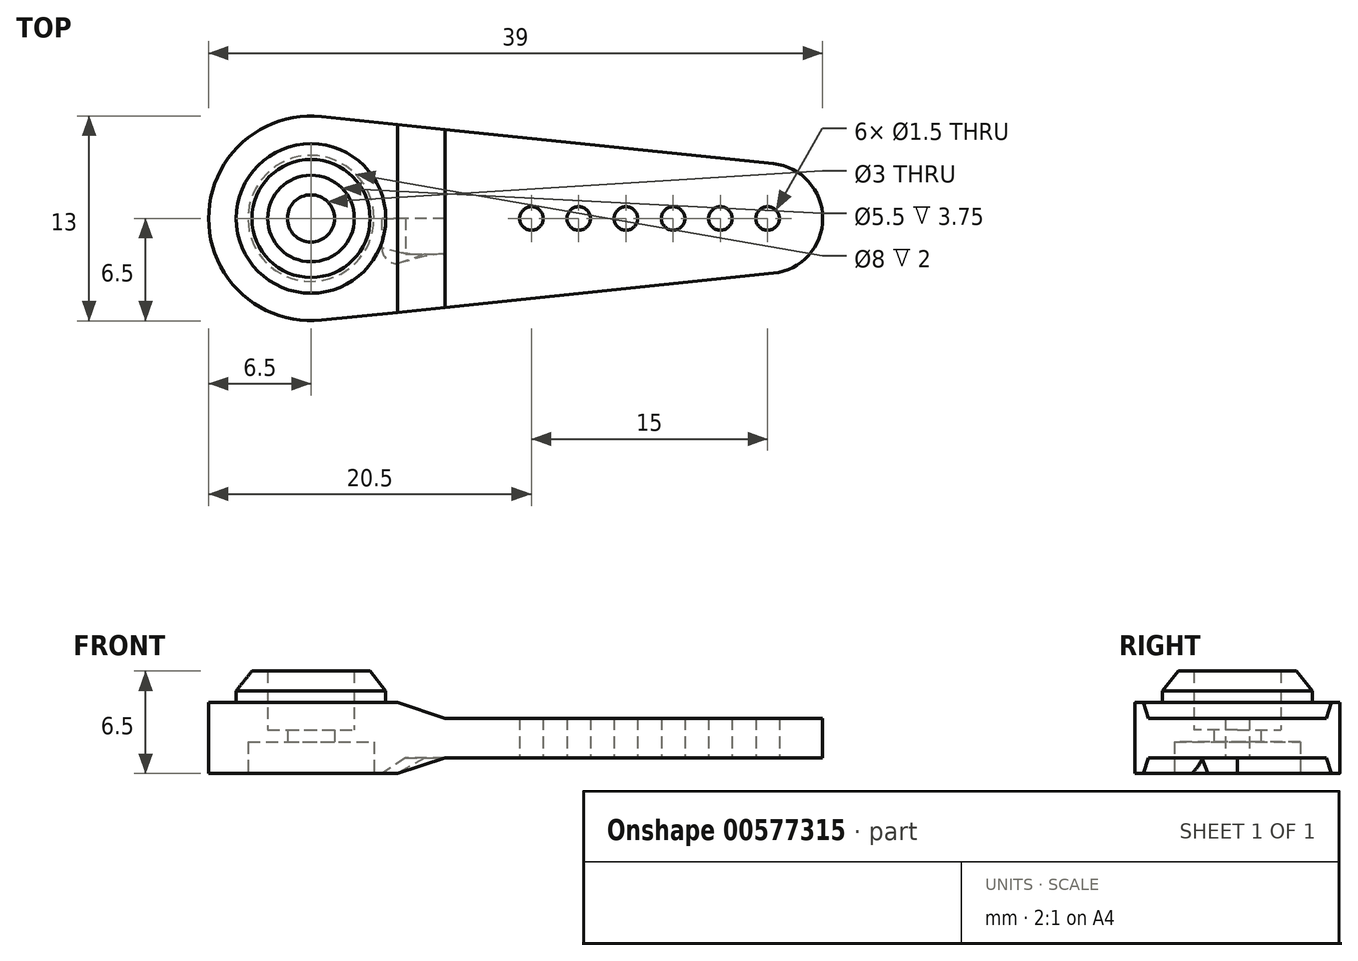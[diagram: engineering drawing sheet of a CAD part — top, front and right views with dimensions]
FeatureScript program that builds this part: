
annotation { "Feature Type Name" : "Feature", "Feature Type Description" : "" }
export const myFeature = defineFeature(function(context is Context, id is Id, definition is map)
    precondition{}
    {
        {
            var Q0;
            Q0=qCreatedBy(makeId("Top.planeOp"),FACE);
            var sketch = newSketch(context, id + "F0", { "sketchPlane" : qUnion([Q0])});
            skLineSegment(sketch, "E0.bottom", {"start": v(0, 0) * mm, "end": v(39, 0) * mm, "construction": true});
            skLineSegment(sketch, "E0.top", {"start": v(0, 13) * mm, "end": v(39, 13) * mm, "construction": true});
            skLineSegment(sketch, "E0.left", {"start": v(0, 0) * mm, "end": v(0, 13) * mm, "construction": true});
            skLineSegment(sketch, "E0.right", {"start": v(39, 0) * mm, "end": v(39, 13) * mm, "construction": true});
            skCircle(sketch, "E1", {"center": v(6.5, 6.5) * mm, "radius": 6.5 * mm});
            skPoint(sketch, "E1.first.point", {"position": v(0, 6.5) * mm});
            skPoint(sketch, "E1.second.point", {"position": v(6.5, 13) * mm});
            skPoint(sketch, "E1.third.point", {"position": v(6.5, 0) * mm});
            skCircle(sketch, "E2", {"center": v(35.5, 6.5) * mm, "radius": 3.5 * mm});
            skLineSegment(sketch, "E3", {"start": v(35.86, 9.98) * mm, "end": v(7.17, 12.97) * mm});
            skLineSegment(sketch, "E4", {"start": v(35.86, 3.02) * mm, "end": v(7.17, 0.03) * mm});
            skCircle(sketch, "E5", {"center": v(35.5, 6.5) * mm, "radius": 0.75 * mm});
            skCircle(sketch, "E6.1.0.0", {"center": v(32.5, 6.5) * mm, "radius": 0.75 * mm});
            skCircle(sketch, "E6.2.0.0", {"center": v(29.5, 6.5) * mm, "radius": 0.75 * mm});
            skCircle(sketch, "E6.3.0.0", {"center": v(26.5, 6.5) * mm, "radius": 0.75 * mm});
            skCircle(sketch, "E6.4.0.0", {"center": v(23.5, 6.5) * mm, "radius": 0.75 * mm});
            skCircle(sketch, "E6.5.0.0", {"center": v(20.5, 6.5) * mm, "radius": 0.75 * mm});
            skLineSegment(sketch, "E6.direction1", {"start": v(35.5, 6.5) * mm, "end": v(32.5, 6.5) * mm, "construction": true});
            skCircle(sketch, "E7", {"center": v(6.5, 6.5) * mm, "radius": 1.5 * mm});
            skSolve(sketch);
        }
        {
            var Q0;
            Q0 = qSketchRegion(id + "F0", true);
            extrude(context, id + "F1", {"entities" : qUnion([Q0]), "depth" : 4.5 * mm, "offsetDistance" : 25 * mm});
        }
        {
            var Q0;
            Q0=qCreatedBy(makeId("Front.planeOp"),FACE);
            var sketch = newSketch(context, id + "F2", { "sketchPlane" : qUnion([Q0])});
            skLineSegment(sketch, "E8", {"start": v(0, 0) * mm, "end": v(0, 2.25) * mm, "construction": true});
            skLineSegment(sketch, "E9", {"start": v(0, 2.25) * mm, "end": v(39, 2.25) * mm, "construction": true});
            skLineSegment(sketch, "E10", {"start": v(39, 2.25) * mm, "end": v(39, 1) * mm, "construction": true});
            skLineSegment(sketch, "E11", {"start": v(0, 0) * mm, "end": v(12, 0) * mm, "construction": true});
            skLineSegment(sketch, "E12", {"start": v(12, 0) * mm, "end": v(15, 1) * mm});
            skLineSegment(sketch, "E13", {"start": v(15, 1) * mm, "end": v(39, 1) * mm});
            skLineSegment(sketch, "E14.MirrorCS", {"start": v(12, 4.5) * mm, "end": v(15, 3.5) * mm});
            skLineSegment(sketch, "E15.MirrorCS", {"start": v(15, 3.5) * mm, "end": v(39, 3.5) * mm});
            skLineSegment(sketch, "E16.MirrorCS", {"start": v(39, 2.25) * mm, "end": v(39, 3.5) * mm, "construction": true});
            skLineSegment(sketch, "E17.MirrorCS", {"start": v(0, 4.5) * mm, "end": v(12, 4.5) * mm, "construction": true});
            skLineSegment(sketch, "E18.MirrorCS", {"start": v(0, 4.5) * mm, "end": v(0, 2.25) * mm, "construction": true});
            skLineSegment(sketch, "E19", {"start": v(12, 4.5) * mm, "end": v(39, 4.5) * mm});
            skLineSegment(sketch, "E20", {"start": v(39, 4.5) * mm, "end": v(39, 3.5) * mm});
            skLineSegment(sketch, "E21", {"start": v(12, 0) * mm, "end": v(39, 0) * mm});
            skLineSegment(sketch, "E22", {"start": v(39, 0) * mm, "end": v(39, 1) * mm});
            skSolve(sketch);
        }
        {
            var Q0;
            Q0 = qSketchRegion(id + "F2", true);
            extrude(context, id + "F3", {"entities" : qUnion([Q0]), "operationType" : NewBodyOperationType.REMOVE, "endBound" : BoundingType.THROUGH_ALL, "oppositeDirection" : true, "depth" : 25 * mm, "offsetDistance" : 25 * mm});
        }
        {
            var Q0;
            Q0=makeQuery(id+"F1.opExtrude","CAP_FACE",FACE,{"disambiguationData":[OSD([sQuery(id+"F0.wireOp",EDGE,"E1"),sQuery(id+"F0.wireOp",EDGE,"E2"),sQuery(id+"F0.wireOp",EDGE,"E3"),sQuery(id+"F0.wireOp",EDGE,"E4"),sQuery(id+"F0.wireOp",EDGE,"E5"),sQuery(id+"F0.wireOp",EDGE,"E6.1.0.0"),sQuery(id+"F0.wireOp",EDGE,"E6.2.0.0"),sQuery(id+"F0.wireOp",EDGE,"E6.3.0.0"),sQuery(id+"F0.wireOp",EDGE,"E6.4.0.0"),sQuery(id+"F0.wireOp",EDGE,"E6.5.0.0"),sQuery(id+"F0.wireOp",EDGE,"E7")])],"isStart":false});
            var sketch = newSketch(context, id + "F4", { "sketchPlane" : qUnion([Q0])});
            skCircle(sketch, "E23", {"center": v(6.5, 6.5) * mm, "radius": 4.75 * mm});
            skCircle(sketch, "E24", {"center": v(6.5, 6.5) * mm, "radius": 2.75 * mm});
            skSolve(sketch);
        }
        {
            var Q0;
            Q0 = qSketchRegion(id + "F4", true);
            extrude(context, id + "F5", {"entities" : qUnion([Q0]), "operationType" : NewBodyOperationType.ADD, "depth" : .75 * mm, "offsetDistance" : 25 * mm});
        }
        {
            var Q0;
            Q0=qCreatedBy(makeId("Front.planeOp"),FACE);
            cPlane(context, id + "F6", {"entities" : qUnion([Q0]), "cplaneType" : CPlaneType.OFFSET, "offset" : 6.5 * mm, "oppositeDirection" : true, "width" : 150 * mm, "height" : 150 * mm});
        }
        {
            var Q0;
            Q0=qCreatedBy(id+"F6.planeOp",FACE);
            var sketch = newSketch(context, id + "F7", { "sketchPlane" : qUnion([Q0])});
            skLineSegment(sketch, "E25.0", {"start": v(1.75, 5.25) * mm, "end": v(11.25, 5.25) * mm, "construction": true});
            skLineSegment(sketch, "E26", {"start": v(11.25, 5.25) * mm, "end": v(9.25, 5.25) * mm});
            skLineSegment(sketch, "E27", {"start": v(9.25, 5.25) * mm, "end": v(9.25, 6.5) * mm});
            skLineSegment(sketch, "E28", {"start": v(9.25, 6.5) * mm, "end": v(10.25, 6.5) * mm});
            skLineSegment(sketch, "E29", {"start": v(10.25, 6.5) * mm, "end": v(11.25, 5.25) * mm});
            skSolve(sketch);
        }
        {
            var Q0;
            Q0=makeQuery(id+"F7.imprint","IMPRINT",FACE,{"disambiguationData":[TD([[makeQuery(id+"F7.imprint","IMPRINT",EDGE,{"derivedFrom":sQuery(id+"F7.wireOp",EDGE,"E26")}),-1.0]])]});
            var Q1;
            Q1=makeQuery(id+"F5.opExtrude","CAP_EDGE",EDGE,{"disambiguationData":[OSD([sQuery(id+"F4.wireOp",EDGE,"E24")])],"isStart":false});
            revolve(context, id + "F8", {"operationType" : NewBodyOperationType.ADD, "entities" : qUnion([Q0]), "axis" : qUnion([Q1]), "revolveType" : RevolveType.FULL});
        }
        {
            var Q0;
            {var subQ0=sQuery(id+"F0.wireOp",EDGE,"E7");Q0=makeQuery(id+"F5.boolean.opBoolean","SPLIT",FACE,{"disambiguationData":[TD([makeQuery(id+"F1.opExtrude","SWEPT_FACE",FACE,{"disambiguationData":[OSD([subQ0])]})])],"derivedFrom":makeQuery(id+"F1.opExtrude","CAP_FACE",FACE,{"disambiguationData":[OSD([sQuery(id+"F0.wireOp",EDGE,"E1"),sQuery(id+"F0.wireOp",EDGE,"E2"),sQuery(id+"F0.wireOp",EDGE,"E3"),sQuery(id+"F0.wireOp",EDGE,"E4"),sQuery(id+"F0.wireOp",EDGE,"E5"),sQuery(id+"F0.wireOp",EDGE,"E6.1.0.0"),sQuery(id+"F0.wireOp",EDGE,"E6.2.0.0"),sQuery(id+"F0.wireOp",EDGE,"E6.3.0.0"),sQuery(id+"F0.wireOp",EDGE,"E6.4.0.0"),sQuery(id+"F0.wireOp",EDGE,"E6.5.0.0"),subQ0])],"isStart":false})});}
            var sketch = newSketch(context, id + "F9", { "sketchPlane" : qUnion([Q0])});
            skCircle(sketch, "E30", {"center": v(6.5, 6.5) * mm, "radius": 2.75 * mm});
            skSolve(sketch);
        }
        {
            var Q0;
            Q0 = qSketchRegion(id + "F9", true);
            extrude(context, id + "F10", {"entities" : qUnion([Q0]), "operationType" : NewBodyOperationType.REMOVE, "oppositeDirection" : true, "depth" : 1.75 * mm, "offsetDistance" : 25 * mm});
        }
        {
            var Q0;
            Q0=makeQuery(id+"F1.opExtrude","CAP_FACE",FACE,{"disambiguationData":[OSD([sQuery(id+"F0.wireOp",EDGE,"E1"),sQuery(id+"F0.wireOp",EDGE,"E2"),sQuery(id+"F0.wireOp",EDGE,"E3"),sQuery(id+"F0.wireOp",EDGE,"E4"),sQuery(id+"F0.wireOp",EDGE,"E5"),sQuery(id+"F0.wireOp",EDGE,"E6.1.0.0"),sQuery(id+"F0.wireOp",EDGE,"E6.2.0.0"),sQuery(id+"F0.wireOp",EDGE,"E6.3.0.0"),sQuery(id+"F0.wireOp",EDGE,"E6.4.0.0"),sQuery(id+"F0.wireOp",EDGE,"E6.5.0.0"),sQuery(id+"F0.wireOp",EDGE,"E7")])],"isStart":true});
            var sketch = newSketch(context, id + "F11", { "sketchPlane" : qUnion([Q0])});
            skCircle(sketch, "E31", {"center": v(6.5, -6.5) * mm, "radius": 4 * mm});
            skSolve(sketch);
        }
        {
            var Q0;
            Q0 = qSketchRegion(id + "F11", true);
            extrude(context, id + "F12", {"entities" : qUnion([Q0]), "operationType" : NewBodyOperationType.REMOVE, "oppositeDirection" : true, "depth" : 2 * mm, "offsetDistance" : 25 * mm});
        }
        {
            var Q0;
            Q0=makeQuery(id+"F3.boolean.opBoolean","COPY",FACE,{"derivedFrom":makeQuery(id+"F3.opExtrude","SWEPT_FACE",FACE,{"disambiguationData":[OSD([sQuery(id+"F2.wireOp",EDGE,"E13")])]})});
            var sketch = newSketch(context, id + "F13", { "sketchPlane" : qUnion([Q0])});
            skLineSegment(sketch, "E32", {"start": v(15, -6.5) * mm, "end": v(12.5, -6.5) * mm});
            skLineSegment(sketch, "E33", {"start": v(12.5, -6.5) * mm, "end": v(12.5, -4.25) * mm});
            skLineSegment(sketch, "E34", {"start": v(12.5, -4.25) * mm, "end": v(15, -4.25) * mm});
            skLineSegment(sketch, "E35", {"start": v(15, -4.25) * mm, "end": v(15, -6.5) * mm});
            skPoint(sketch, "E36.orphan", {"position": v(39, -6.5) * mm});
            skSolve(sketch);
        }
        {
            var Q0;
            Q0=makeQuery(id+"F1.opExtrude","CAP_FACE",FACE,{"disambiguationData":[OSD([sQuery(id+"F0.wireOp",EDGE,"E1"),sQuery(id+"F0.wireOp",EDGE,"E2"),sQuery(id+"F0.wireOp",EDGE,"E3"),sQuery(id+"F0.wireOp",EDGE,"E4"),sQuery(id+"F0.wireOp",EDGE,"E5"),sQuery(id+"F0.wireOp",EDGE,"E6.1.0.0"),sQuery(id+"F0.wireOp",EDGE,"E6.2.0.0"),sQuery(id+"F0.wireOp",EDGE,"E6.3.0.0"),sQuery(id+"F0.wireOp",EDGE,"E6.4.0.0"),sQuery(id+"F0.wireOp",EDGE,"E6.5.0.0"),sQuery(id+"F0.wireOp",EDGE,"E7")])],"isStart":true});
            var sketch = newSketch(context, id + "F14", { "sketchPlane" : qUnion([Q0])});
            skPoint(sketch, "E37.0", {"position": v(15, -4.25) * mm});
            skPoint(sketch, "E38.0", {"position": v(15, -8.75) * mm});
            skLineSegment(sketch, "E39", {"start": v(15, -4.25) * mm, "end": v(12, -3.63) * mm});
            skLineSegment(sketch, "E40", {"start": v(15, -4.25) * mm, "end": v(15, -6.5) * mm});
            skLineSegment(sketch, "E41", {"start": v(12, -3.63) * mm, "end": v(12, -3.63) * mm});
            skLineSegment(sketch, "E42", {"start": v(11, -4.63) * mm, "end": v(11, -6.5) * mm});
            skLineSegment(sketch, "E43", {"start": v(12, -9.38) * mm, "end": v(12, -9.38) * mm});
            skPoint(sketch, "E44.visualSharp", {"position": v(11, -3.63) * mm});
            skArc(sketch, "E44.filletArc", {"start": v(12, -3.63) * mm, "mid": v(11.3, -3.92) * mm, "end": v(11, -4.63) * mm});
            skPoint(sketch, "E45.visualSharp", {"position": v(11, -9.38) * mm});
            skPoint(sketch, "E46", {"position": v(11, -6.5) * mm});
            skLineSegment(sketch, "E47", {"start": v(11, -6.5) * mm, "end": v(15, -6.5) * mm});
            skPoint(sketch, "E45.filletArc.start.orphan", {"position": v(11, -8.38) * mm});
            skSolve(sketch);
        }
        {
            var Q0;
            Q0=qCreatedBy(id+"F6.planeOp",FACE);
            var sketch = newSketch(context, id + "F15", { "sketchPlane" : qUnion([Q0])});
            skPoint(sketch, "E48.0", {"position": v(15, 0) * mm});
            skPoint(sketch, "E49.0", {"position": v(15, 1) * mm});
            skPoint(sketch, "E50.0", {"position": v(12.5, 1) * mm});
            skPoint(sketch, "E51.0", {"position": v(11, 0) * mm});
            skLineSegment(sketch, "E52", {"start": v(15, 1) * mm, "end": v(15, 0) * mm});
            skLineSegment(sketch, "E53", {"start": v(12.5, 1) * mm, "end": v(11, 0) * mm});
            skSolve(sketch);
        }
        {
            var Q1;
            Q1 = qSketchRegion(id + "F13", true);
            var Q2;
            Q2 = qSketchRegion(id + "F14", true);
            var Q3;
            Q3=sQuery(id+"F15.wireOp",EDGE,"E52");
            var Q4;
            Q4=sQuery(id+"F15.wireOp",EDGE,"E53");
            loft(context, id + "F16", {"operationType" : NewBodyOperationType.REMOVE, "addGuides" : true, "sheetProfilesArray" : [{ "sheetProfileEntities" : qUnion([Q1]) }, { "sheetProfileEntities" : qUnion([Q2]) }], "guidesArray" : [{ "guideEntities" : qUnion([Q3]), "guideDerivativeType" : LoftGuideDerivativeType.DEFAULT, "guideDerivativeMagnitude" : 1 }, { "guideEntities" : qUnion([Q4]), "guideDerivativeType" : LoftGuideDerivativeType.DEFAULT, "guideDerivativeMagnitude" : 1 }]});
        }
    });
